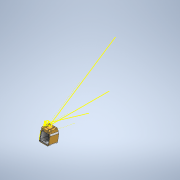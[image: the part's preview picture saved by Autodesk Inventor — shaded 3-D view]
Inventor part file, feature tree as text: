
AUTODESK INVENTOR PART (.ipt)
format: ipt  version: 2020 (Build 240168000, 168)  size: 329,728 bytes
history: native  units: mm
features: sketch x8, other x3, projected_geometry x2, extrude x1
ambient origin geometry x8: Origin, YZ Plane, XZ Plane, XY Plane, X Axis, Y Axis, Z Axis, Center Point
bodies: Solid1 (feature_tree)
feature tree (14):
  other  "V2 modular session with camera for cutout 50 deg.iam"
  other  "V2 session mount 50deg block.ipt:1"
  other  "50 deg predator nano mount.ipt:1"
  extrude  "Extrusion1"  Depth=10.0mm TaperAngle=0.0deg
  sketch  "Sketch6"
  sketch  "Sketch7"
  sketch  "Sketch1"  dims[d0=10.0mm d1=10.0mm d2=0.0mm]
  sketch  "Sketch1_1"
  sketch  "Sketch6_1"
  sketch  "Sketch10"
  sketch  "Sketch11"
  sketch  "Sketch12"
  projected_geometry  "Projected Loop1"
  projected_geometry  "Projected Loop2"
